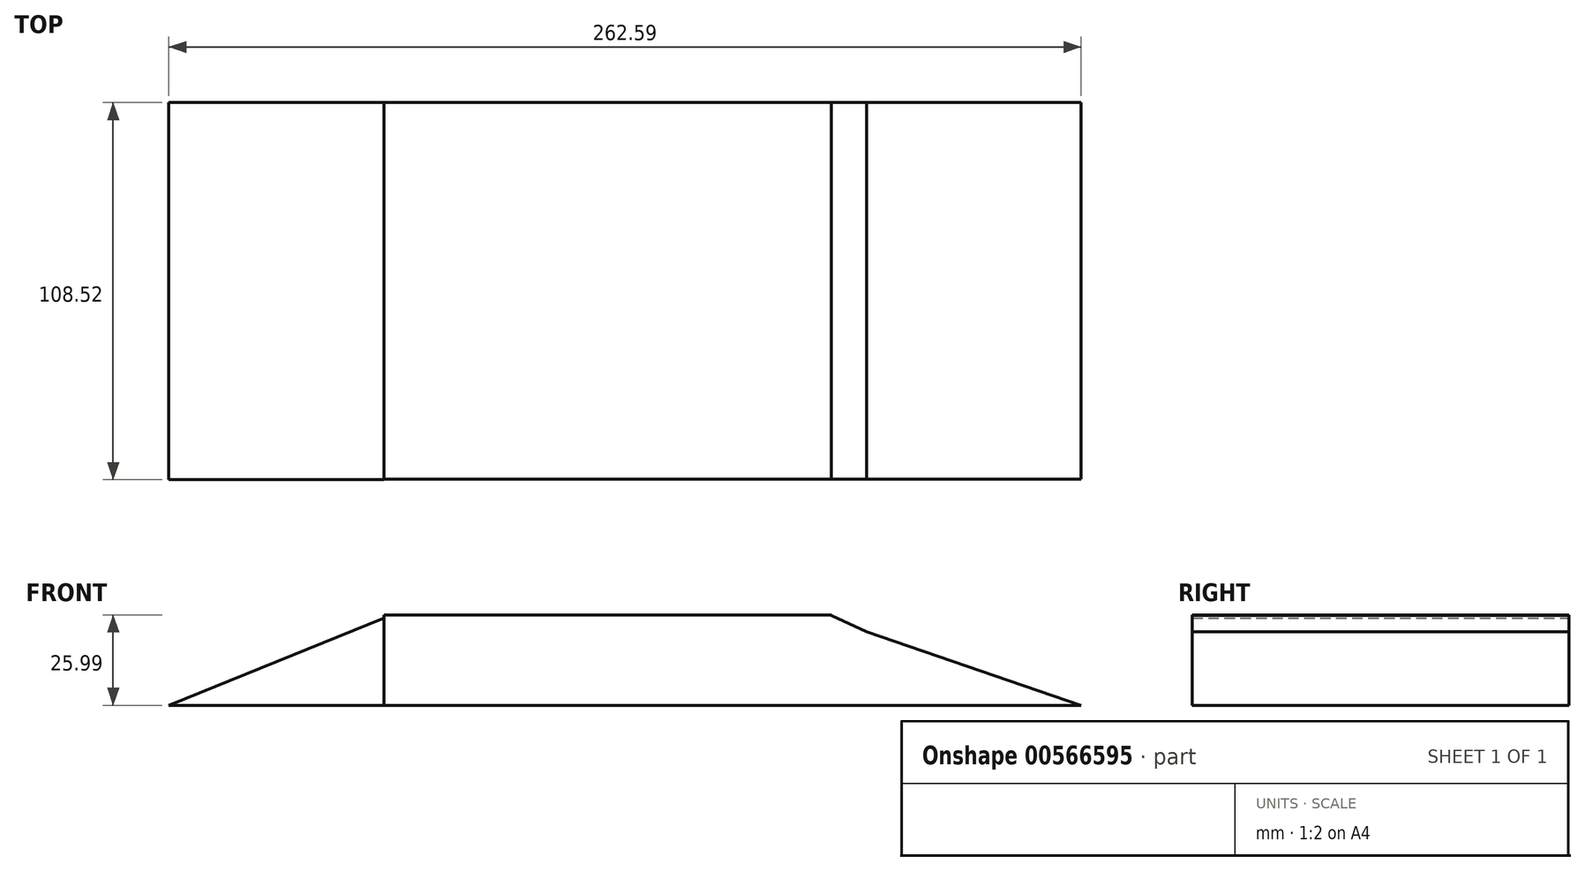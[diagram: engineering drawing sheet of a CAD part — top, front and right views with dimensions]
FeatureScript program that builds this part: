
annotation { "Feature Type Name" : "Feature", "Feature Type Description" : "" }
export const myFeature = defineFeature(function(context is Context, id is Id, definition is map)
    precondition{}
    {
        {
            var Q0;
            Q0=qCreatedBy(makeId("Front.planeOp"),FACE);
            var sketch = newSketch(context, id + "F0", { "sketchPlane" : qUnion([Q0])});
            skLineSegment(sketch, "E0.bottom", {"start": v(0, 0) * mm, "end": v(128.72, 0) * mm});
            skLineSegment(sketch, "E0.top", {"start": v(0, 25.99) * mm, "end": v(128.72, 25.99) * mm});
            skLineSegment(sketch, "E0.left", {"start": v(0, 0) * mm, "end": v(0, 25.99) * mm});
            skLineSegment(sketch, "E0.right", {"start": v(128.72, 0) * mm, "end": v(128.72, 25.99) * mm});
            skSolve(sketch);
        }
        {
            var Q0;
            Q0=qCreatedBy(makeId("Front.planeOp"),FACE);
            var sketch = newSketch(context, id + "F1", { "sketchPlane" : qUnion([Q0])});
            skLineSegment(sketch, "E1", {"start": v(0, 26) * mm, "end": v(-61.7, 0) * mm});
            skLineSegment(sketch, "E2", {"start": v(-61.7, 0) * mm, "end": v(0, 0) * mm});
            skSolve(sketch);
        }
        {
            var Q0;
            Q0=qCreatedBy(makeId("Front.planeOp"),FACE);
            var sketch = newSketch(context, id + "F2", { "sketchPlane" : qUnion([Q0])});
            skLineSegment(sketch, "E3", {"start": v(129.54, 13.14) * mm, "end": v(205.23, 0) * mm});
            skLineSegment(sketch, "E4", {"start": v(205.23, 0) * mm, "end": v(129.54, 0) * mm});
            skSolve(sketch);
        }
        {
            var Q0;
            Q0=qCreatedBy(makeId("Front.planeOp"),FACE);
            var sketch = newSketch(context, id + "F3", { "sketchPlane" : qUnion([Q0])});
            skLineSegment(sketch, "E5", {"start": v(128.98, 26.69) * mm, "end": v(205.55, 0) * mm});
            skSolve(sketch);
        }
        {
            var Q0;
            Q0=qCreatedBy(makeId("Front.planeOp"),FACE);
            var sketch = newSketch(context, id + "F4", { "sketchPlane" : qUnion([Q0])});
            skLineSegment(sketch, "E6", {"start": v(130.38, 13.4) * mm, "end": v(0, 13.4) * mm});
            skSolve(sketch);
        }
        {
            var Q0;
            Q0 = qSketchRegion(id + "F1", true);
            var Q1;
            Q1 = qSketchRegion(id + "F4", true);
            var Q2;
            Q2 = qSketchRegion(id + "F0", true);
            var Q3;
            Q3=makeQuery(id+"F0.imprint","IMPRINT",FACE,{"disambiguationData":[TD([[makeQuery(id+"F0.imprint","IMPRINT",EDGE,{"derivedFrom":sQuery(id+"F0.wireOp",EDGE,"E0.bottom")}),1.0]])]});
            var Q4;
            Q4 = qSketchRegion(id + "F3", true);
            var Q5;
            Q5 = qSketchRegion(id + "F2", true);
            extrude(context, id + "F5", {"entities" : qUnion([Q0, Q1, Q2, Q3, Q4, Q5]), "depth" : 25.4 * mm, "offsetDistance" : 25.4 * mm});
        }
        {
            var Q0;
            Q0=qCreatedBy(makeId("Front.planeOp"),FACE);
            var sketch = newSketch(context, id + "F6", { "sketchPlane" : qUnion([Q0])});
            skLineSegment(sketch, "E7", {"start": v(128.57, 25.88) * mm, "end": v(160.31, 0) * mm});
            skLineSegment(sketch, "E8", {"start": v(160.31, 0) * mm, "end": v(160.31, 0) * mm});
            skLineSegment(sketch, "E9", {"start": v(128.57, 25.88) * mm, "end": v(185.96, 0) * mm});
            skLineSegment(sketch, "E10", {"start": v(185.96, 0) * mm, "end": v(127.97, 0) * mm});
            skLineSegment(sketch, "E11", {"start": v(127.97, 0) * mm, "end": v(128.57, 25.88) * mm});
            skSolve(sketch);
        }
        {
            var Q0;
            Q0 = qSketchRegion(id + "F6", true);
            var sketch = newSketch(context, id + "F7", { "sketchPlane" : qUnion([Q0])});
            skLineSegment(sketch, "E12", {"start": v(128.02, 24.96) * mm, "end": v(200.66, 0) * mm});
            skLineSegment(sketch, "E13", {"start": v(200.66, 0) * mm, "end": v(122.78, 0) * mm});
            skLineSegment(sketch, "E14", {"start": v(122.78, 0) * mm, "end": v(122.78, 24.96) * mm});
            skLineSegment(sketch, "E15", {"start": v(122.78, 24.96) * mm, "end": v(128.02, 24.96) * mm});
            skSolve(sketch);
        }
        {
            var Q0;
            Q0 = qSketchRegion(id + "F6", true);
            var Q1;
            Q1 = qSketchRegion(id + "F2", true);
            var Q2;
            {var subQ0=sQuery(id+"F6.wireOp",EDGE,"E7");Q2=makeQuery(id+"F6.imprint","IMPRINT",FACE,{"disambiguationData":[TD([[makeQuery(id+"F6.imprint","IMPRINT",EDGE,{"derivedFrom":subQ0}),1.0]])]});}
            var Q3;
            {var subQ0=sQuery(id+"F6.wireOp",EDGE,"E7");Q3=makeQuery(id+"F6.imprint","IMPRINT",FACE,{"disambiguationData":[TD([[makeQuery(id+"F6.imprint","IMPRINT",EDGE,{"derivedFrom":subQ0}),-1.0]])]});}
            var Q4;
            {var subQ0=sQuery(id+"F7.wireOp",EDGE,"E13");var subQ1=sQuery(id+"F7.wireOp",EDGE,"E12");var subQ2=makeQuery(id+"F7.imprint","INTERSECT",VERTEX,{"derivedFrom":[subQ1,subQ0]});Q4=makeQuery(id+"F7.imprint","IMPRINT",FACE,{"disambiguationData":[TD([[makeQuery(id+"F7.imprint","IMPRINT",EDGE,{"disambiguationData":[TD([[subQ2,1.0]])],"derivedFrom":subQ1}),-1.0]])]});}
            extrude(context, id + "F8", {"entities" : qUnion([Q0, Q1, Q2, Q3, Q4]), "operationType" : NewBodyOperationType.ADD, "depth" : 25.4 * mm, "offsetDistance" : 25.4 * mm});
        }
        {
            var Q0;
            {var subQ0=sQuery(id+"F6.wireOp",EDGE,"E9");Q0=makeQuery(id+"F8.boolean.opBoolean","MERGE",FACE,{"derivedFrom":[makeQuery(id+"F5.opExtrude","CAP_FACE",FACE,{"disambiguationData":[OSD([sQuery(id+"F0.wireOp",EDGE,"E0.bottom"),sQuery(id+"F0.wireOp",EDGE,"E0.top"),sQuery(id+"F0.wireOp",EDGE,"E0.left"),sQuery(id+"F0.wireOp",EDGE,"E0.right")])],"isStart":false}),makeQuery(id+"F8.opExtrude","CAP_FACE",FACE,{"disambiguationData":[OSD([subQ0,sQuery(id+"F6.wireOp",EDGE,"E10"),sQuery(id+"F6.wireOp",EDGE,"E11")])],"isStart":false}),makeQuery(id+"F8.opExtrude","CAP_FACE",FACE,{"disambiguationData":[OSD([subQ0,sQuery(id+"F7.wireOp",EDGE,"E12"),sQuery(id+"F7.wireOp",EDGE,"E13")])],"isStart":false})]});}
            extrude(context, id + "F9", {"entities" : qUnion([Q0]), "operationType" : NewBodyOperationType.ADD, "depth" : 83.06 * mm, "offsetDistance" : 25.4 * mm});
        }
        {
            var Q0;
            Q0=qCreatedBy(makeId("Front.planeOp"),FACE);
            var sketch = newSketch(context, id + "F10", { "sketchPlane" : qUnion([Q0])});
            skLineSegment(sketch, "E16", {"start": v(0, 25.08) * mm, "end": v(-61.93, 0) * mm});
            skLineSegment(sketch, "E17", {"start": v(-61.93, 0) * mm, "end": v(0, 0) * mm});
            skLineSegment(sketch, "E18", {"start": v(0, 0) * mm, "end": v(0, 25.08) * mm});
            skSolve(sketch);
        }
        {
            var Q0;
            Q0=makeQuery(id+"F10.imprint","IMPRINT",FACE,{"disambiguationData":[TD([[makeQuery(id+"F10.imprint","IMPRINT",EDGE,{"derivedFrom":sQuery(id+"F10.wireOp",EDGE,"E16")}),1.0]])]});
            extrude(context, id + "F11", {"entities" : qUnion([Q0]), "operationType" : NewBodyOperationType.ADD, "depth" : 108.52 * mm, "offsetDistance" : 25.4 * mm});
        }
    });
